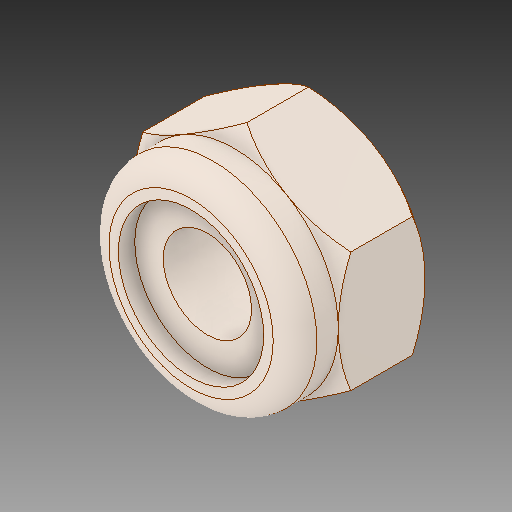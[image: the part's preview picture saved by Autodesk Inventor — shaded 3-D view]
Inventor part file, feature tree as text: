
AUTODESK INVENTOR PART (.ipt)
format: ipt  version: 2018 (Build 220112000, 112)  size: 167,936 bytes
history: native  units: in
note: dims shown in document units (in); Inventor stores cm internally (conversion verified against a paired STEP export)
features: fillet x1
ambient origin geometry x8: Origin, YZ Plane, XZ Plane, XY Plane, X Axis, Y Axis, Z Axis, Center Point
bodies: Solid1 (feature_tree)
feature tree (1):
  fillet  "Fillet1"  [1 undecoded]
note: 1 required parameter value undecoded (feature->parameter linkage not recoverable at this tier; creation-order binding heuristic only, values carry confidence <= 0.55)
